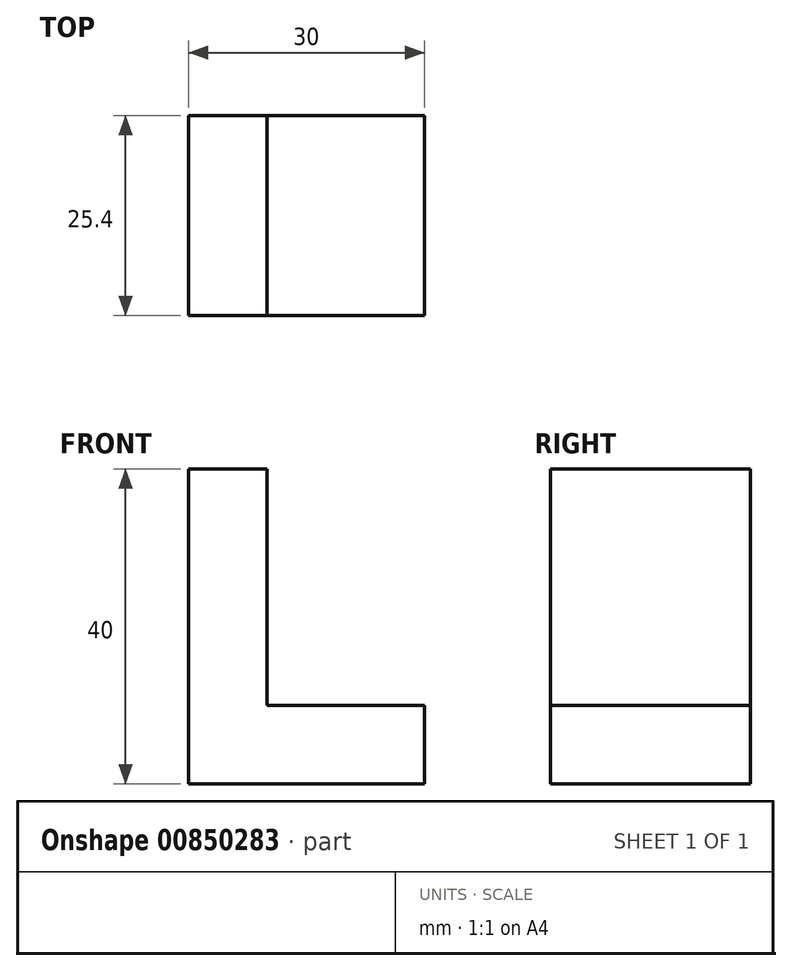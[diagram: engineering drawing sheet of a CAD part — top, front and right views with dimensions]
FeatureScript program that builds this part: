
annotation { "Feature Type Name" : "Feature", "Feature Type Description" : "" }
export const myFeature = defineFeature(function(context is Context, id is Id, definition is map)
    precondition{}
    {
        {
            var Q0;
            Q0=qCreatedBy(makeId("Front.planeOp"),FACE);
            var sketch = newSketch(context, id + "F0", { "sketchPlane" : qUnion([Q0])});
            skLineSegment(sketch, "E0.bottom", {"start": v(-15, 5) * mm, "end": v(15, 5) * mm});
            skLineSegment(sketch, "E0.top", {"start": v(-15, -5) * mm, "end": v(15, -5) * mm});
            skLineSegment(sketch, "E0.left", {"start": v(-15, 5) * mm, "end": v(-15, -5) * mm});
            skLineSegment(sketch, "E0.right", {"start": v(15, 5) * mm, "end": v(15, -5) * mm});
            skPoint(sketch, "E0.middle", {"position": v(0, 0) * mm});
            skLineSegment(sketch, "E1.bottom", {"start": v(-15, 5) * mm, "end": v(-5, 5) * mm});
            skLineSegment(sketch, "E1.top", {"start": v(-15, 35) * mm, "end": v(-5, 35) * mm});
            skLineSegment(sketch, "E1.left", {"start": v(-15, 5) * mm, "end": v(-15, 35) * mm});
            skLineSegment(sketch, "E1.right", {"start": v(-5, 5) * mm, "end": v(-5, 35) * mm});
            skSolve(sketch);
        }
        {
            var Q0;
            Q0 = qSketchRegion(id + "F0", true);
            extrude(context, id + "F1", {"entities" : qUnion([Q0]), "endBound" : BoundingType.SYMMETRIC, "depth" : 25.4 * mm, "offsetDistance" : 25.4 * mm});
        }
    });
